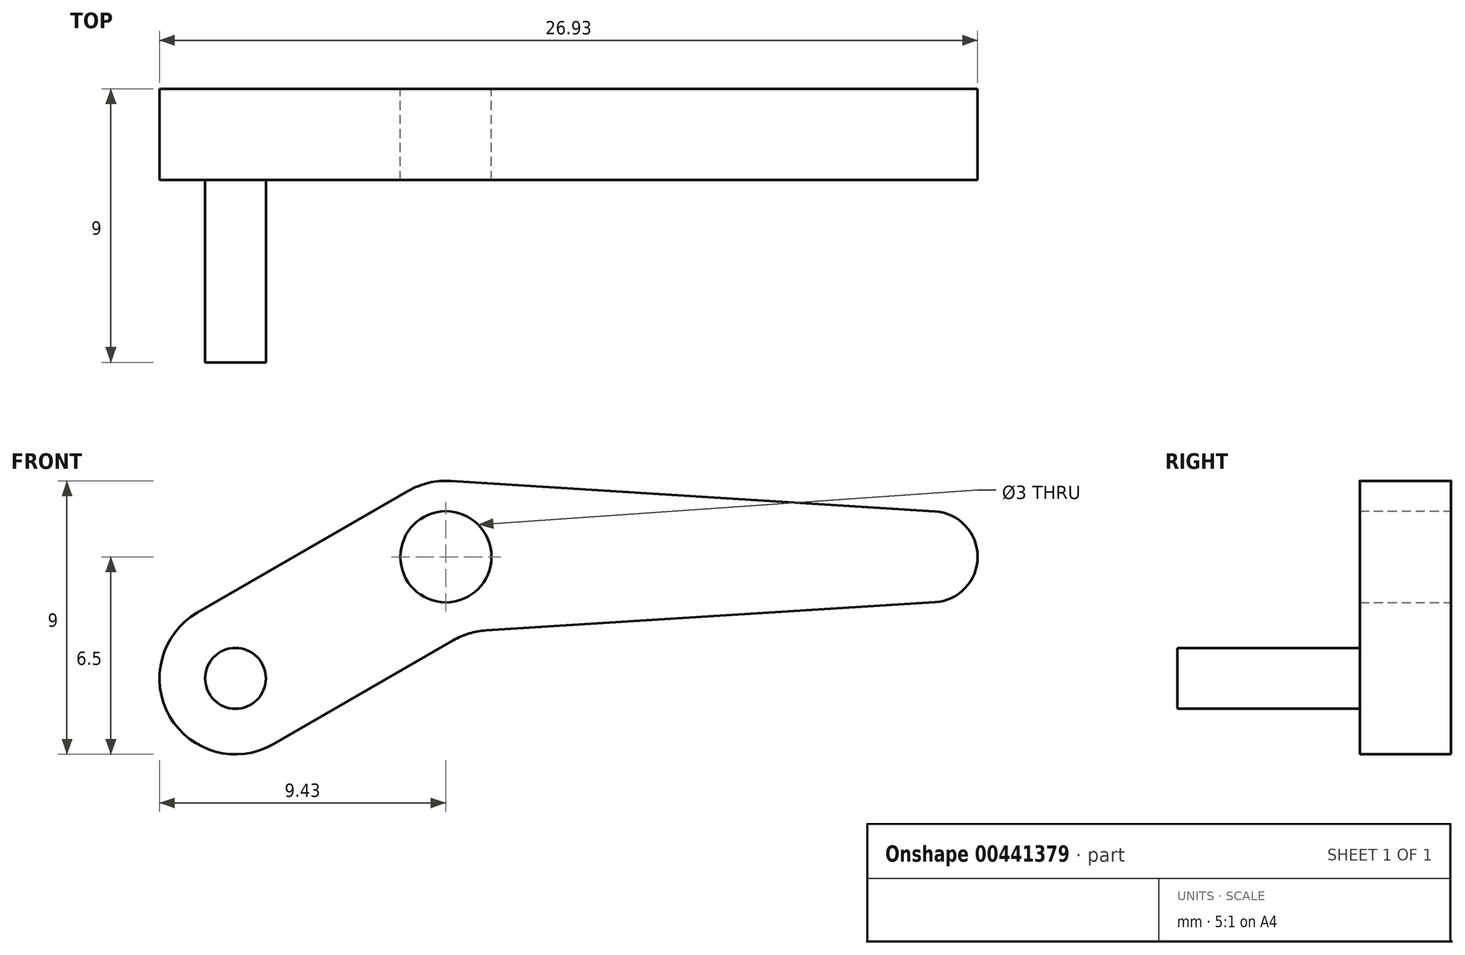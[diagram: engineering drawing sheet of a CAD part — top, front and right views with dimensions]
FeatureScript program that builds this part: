
annotation { "Feature Type Name" : "Feature", "Feature Type Description" : "" }
export const myFeature = defineFeature(function(context is Context, id is Id, definition is map)
    precondition{}
    {
        {
            var Q0;
            Q0=qCreatedBy(makeId("Front.planeOp"),FACE);
            var sketch = newSketch(context, id + "F0", { "sketchPlane" : qUnion([Q0])});
            skArc(sketch, "E0", {"start": v(1.25, 2.17) * mm, "mid": v(0.57, 2.43) * mm, "end": v(-0.16, 2.5) * mm});
            skArc(sketch, "E1", {"start": v(-16.1, 1.5) * mm, "mid": v(-17.5, 0) * mm, "end": v(-16.1, -1.5) * mm});
            skLineSegment(sketch, "E2", {"start": v(-16.1, 1.5) * mm, "end": v(-0.16, 2.5) * mm});
            skPoint(sketch, "E3.orphan", {"position": v(-40, 0) * mm});
            skLineSegment(sketch, "E4", {"start": v(-16.1, -1.5) * mm, "end": v(-1.33, -2.42) * mm});
            skCircle(sketch, "E5", {"center": v(0, 0) * mm, "radius": 1.5 * mm});
            skLineSegment(sketch, "E6", {"start": v(1.25, 2.17) * mm, "end": v(8.18, -1.83) * mm});
            skLineSegment(sketch, "E7", {"start": v(-0.23, -2.75) * mm, "end": v(5.68, -6.17) * mm});
            skArc(sketch, "E8", {"start": v(5.68, -6.17) * mm, "mid": v(9.1, -5.25) * mm, "end": v(8.18, -1.83) * mm});
            skPoint(sketch, "E9.visualSharp", {"position": v(-0.74, -2.46) * mm});
            skArc(sketch, "E9.filletArc", {"start": v(-0.23, -2.75) * mm, "mid": v(-0.76, -2.52) * mm, "end": v(-1.33, -2.42) * mm});
            skSolve(sketch);
        }
        {
            var Q0;
            Q0=qSketchRegion(id+"F0",true);
            extrude(context, id + "F1", {"entities" : qUnion([Q0]), "depth" : 3 * mm});
        }
        {
            var Q0;
            Q0=makeQuery(id+"F1.opExtrude","CAP_FACE",FACE,{"disambiguationData":[OSD([sQuery(id+"F0.wireOp",EDGE,"E0"),sQuery(id+"F0.wireOp",EDGE,"E1"),sQuery(id+"F0.wireOp",EDGE,"E2"),sQuery(id+"F0.wireOp",EDGE,"E4"),sQuery(id+"F0.wireOp",EDGE,"E5"),sQuery(id+"F0.wireOp",EDGE,"E6"),sQuery(id+"F0.wireOp",EDGE,"E7"),sQuery(id+"F0.wireOp",EDGE,"E8"),sQuery(id+"F0.wireOp",EDGE,"E9.filletArc")])],"isStart":false});
            var sketch = newSketch(context, id + "F2", { "sketchPlane" : qUnion([Q0])});
            skCircle(sketch, "E10", {"center": v(6.93, -4) * mm, "radius": 1 * mm});
            skSolve(sketch);
        }
        {
            var Q0;
            Q0=qSketchRegion(id+"F2",true);
            extrude(context, id + "F3", {"entities" : qUnion([Q0]), "operationType" : NewBodyOperationType.ADD, "depth" : 6 * mm});
        }
        {
            var Q0;
            Q0=makeQuery(id+"F1.opExtrude","SWEPT_BODY",BODY,{"disambiguationData":[OSD([sQuery(id+"F0.wireOp",EDGE,"E0"),sQuery(id+"F0.wireOp",EDGE,"E1"),sQuery(id+"F0.wireOp",EDGE,"E2"),sQuery(id+"F0.wireOp",EDGE,"E4"),sQuery(id+"F0.wireOp",EDGE,"E5"),sQuery(id+"F0.wireOp",EDGE,"E6"),sQuery(id+"F0.wireOp",EDGE,"E7"),sQuery(id+"F0.wireOp",EDGE,"E8"),sQuery(id+"F0.wireOp",EDGE,"E9.filletArc")])]});
            var Q1;
            Q1=qCreatedBy(makeId("Right.planeOp"),FACE);
            mirror(context, id + "F4", {"entities" : qUnion([Q0]), "mirrorPlane" : qUnion([Q1])});
        }
        {
            var Q0;
            Q0=makeQuery(id+"F1.opExtrude","SWEPT_BODY",BODY,{"disambiguationData":[OSD([sQuery(id+"F0.wireOp",EDGE,"E0"),sQuery(id+"F0.wireOp",EDGE,"E1"),sQuery(id+"F0.wireOp",EDGE,"E2"),sQuery(id+"F0.wireOp",EDGE,"E4"),sQuery(id+"F0.wireOp",EDGE,"E5"),sQuery(id+"F0.wireOp",EDGE,"E6"),sQuery(id+"F0.wireOp",EDGE,"E7"),sQuery(id+"F0.wireOp",EDGE,"E8"),sQuery(id+"F0.wireOp",EDGE,"E9.filletArc")])]});
            deleteBodies(context, id + "F5", {"entities" : qUnion([Q0])});
        }
    });
